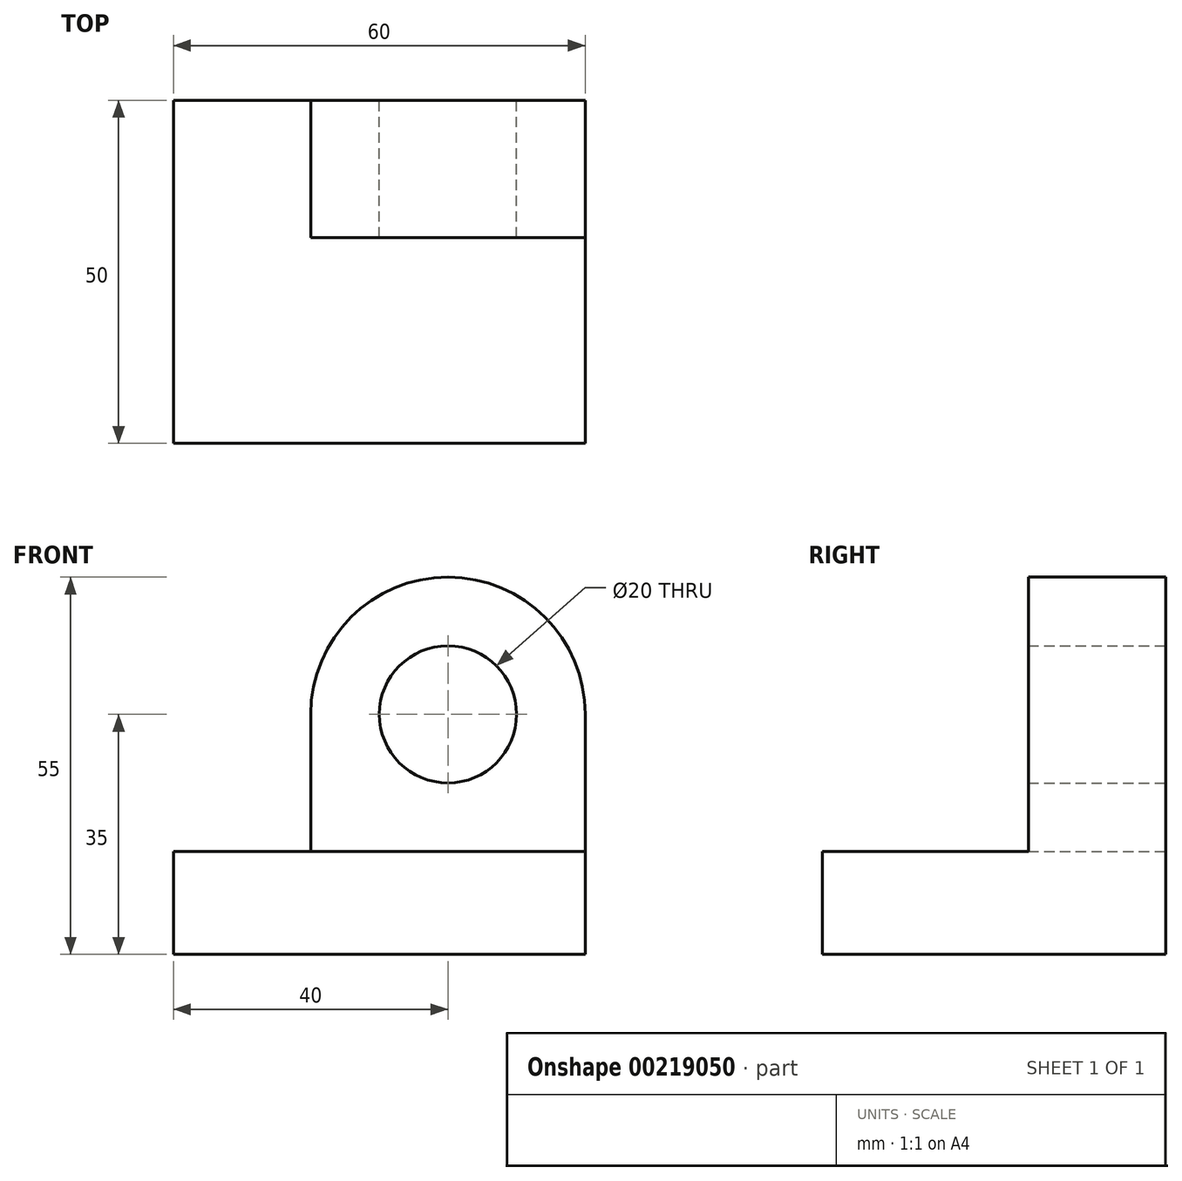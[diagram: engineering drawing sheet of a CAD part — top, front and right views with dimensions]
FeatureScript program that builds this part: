
annotation { "Feature Type Name" : "Feature", "Feature Type Description" : "" }
export const myFeature = defineFeature(function(context is Context, id is Id, definition is map)
    precondition{}
    {
        {
            var Q0;
            Q0=qCreatedBy(makeId("Front.planeOp"),FACE);
            var sketch = newSketch(context, id + "F0", { "sketchPlane" : qUnion([Q0])});
            skLineSegment(sketch, "E0", {"start": v(0, 0) * mm, "end": v(60, 0) * mm});
            skLineSegment(sketch, "E1", {"start": v(60, 0) * mm, "end": v(60, 15) * mm});
            skLineSegment(sketch, "E2", {"start": v(60, 15) * mm, "end": v(0, 15) * mm});
            skLineSegment(sketch, "E3", {"start": v(0, 15) * mm, "end": v(0, 0) * mm});
            skCircle(sketch, "E4", {"center": v(40, 35) * mm, "radius": 10 * mm});
            skArc(sketch, "E5", {"start": v(60, 35) * mm, "mid": v(40, 55) * mm, "end": v(20, 35) * mm});
            skLineSegment(sketch, "E6", {"start": v(60, 35) * mm, "end": v(60, 15) * mm});
            skLineSegment(sketch, "E7", {"start": v(20, 35) * mm, "end": v(20, 15) * mm});
            skSolve(sketch);
        }
        {
            var Q0;
            Q0=makeQuery(id+"F0.imprint","IMPRINT",FACE,{"disambiguationData":[TD([[makeQuery(id+"F0.imprint","IMPRINT",EDGE,{"derivedFrom":sQuery(id+"F0.wireOp",EDGE,"E0")}),1.0]])]});
            extrude(context, id + "F1", {"entities" : qUnion([Q0]), "depth" : 50 * mm});
        }
        {
            var Q0;
            Q0=makeQuery(id+"F0.imprint","IMPRINT",FACE,{"disambiguationData":[TD([[makeQuery(id+"F0.imprint","IMPRINT",EDGE,{"derivedFrom":sQuery(id+"F0.wireOp",EDGE,"E4")}),-1.0]])]});
            extrude(context, id + "F2", {"entities" : qUnion([Q0]), "operationType" : NewBodyOperationType.ADD, "depth" : 20 * mm});
        }
    });
